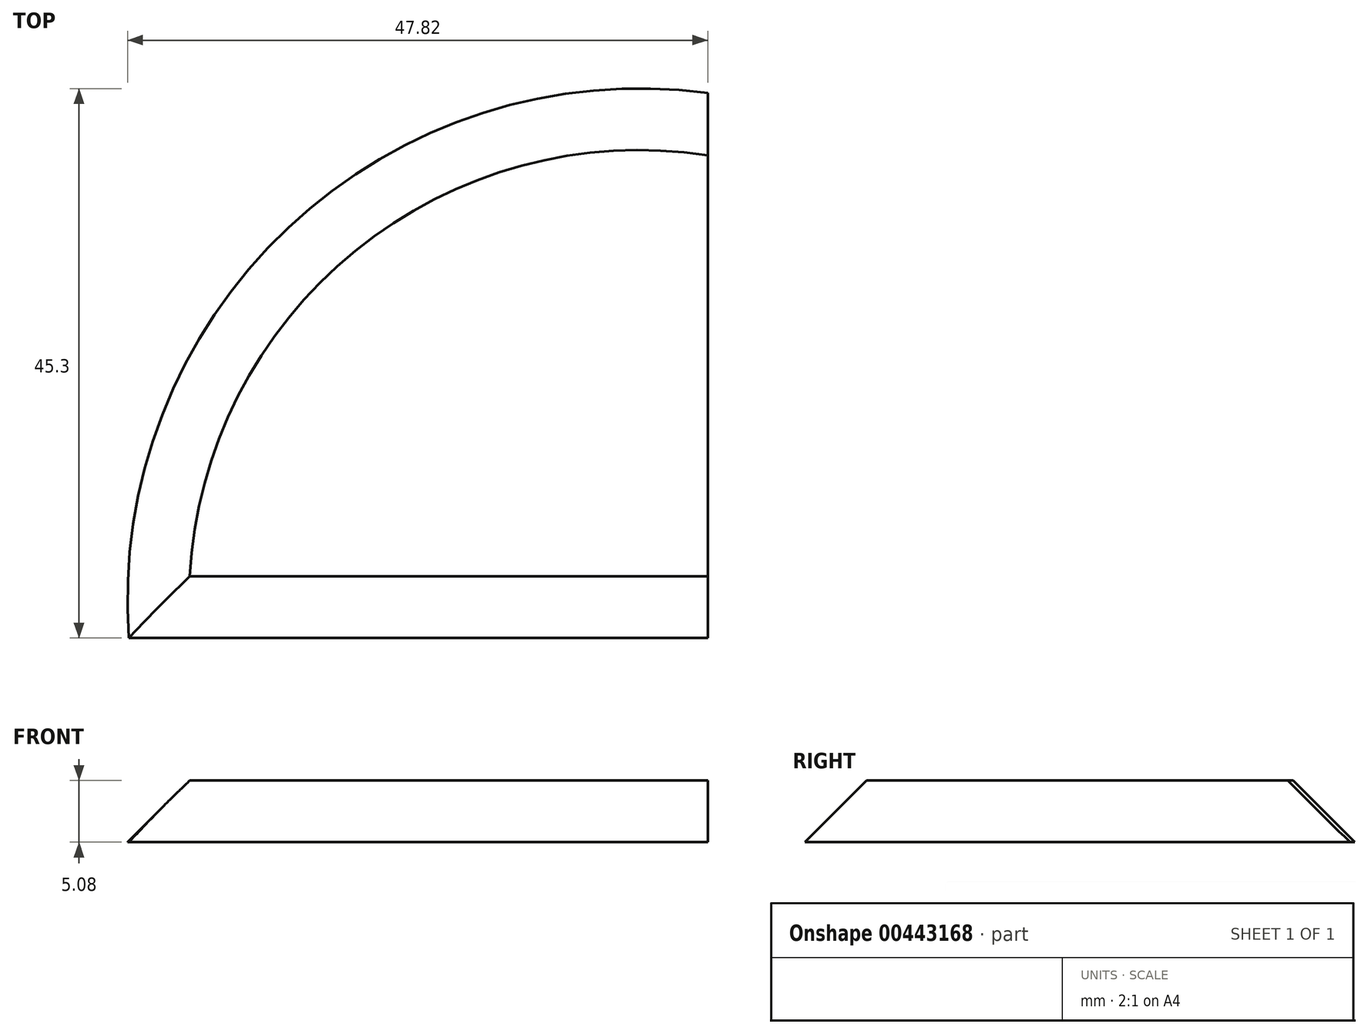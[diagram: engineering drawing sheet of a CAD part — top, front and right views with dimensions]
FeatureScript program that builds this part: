
annotation { "Feature Type Name" : "Feature", "Feature Type Description" : "" }
export const myFeature = defineFeature(function(context is Context, id is Id, definition is map)
    precondition{}
    {
        {
            var Q0;
            Q0=qCreatedBy(makeId("Top.planeOp"),FACE);
            var sketch = newSketch(context, id + "F0", { "sketchPlane" : qUnion([Q0])});
            skArc(sketch, "E0", {"start": v(0, 44.92) * mm, "mid": v(-34.56, 33.84) * mm, "end": v(-47.7, 0) * mm});
            skLineSegment(sketch, "E1", {"start": v(0, 44.92) * mm, "end": v(0, 0) * mm});
            skLineSegment(sketch, "E2", {"start": v(0, 0) * mm, "end": v(-47.7, 0) * mm});
            skSolve(sketch);
        }
        {
            var Q0;
            Q0 = qSketchRegion(id + "F0", true);
            extrude(context, id + "F1", {"entities" : qUnion([Q0]), "depth" : 5.08 * mm});
        }
        {
            var Q0;
            Q0=makeQuery(id+"F1.opExtrude","CAP_EDGE",EDGE,{"disambiguationData":[OSD([sQuery(id+"F0.wireOp",EDGE,"E0")])],"isStart":false});
            var Q1;
            Q1=makeQuery(id+"F1.opExtrude","CAP_EDGE",EDGE,{"disambiguationData":[OSD([sQuery(id+"F0.wireOp",EDGE,"E2")])],"isStart":false});
            chamfer(context, id + "F2", {"entities" : qUnion([Q0, Q1]), "width" : 5.08 * mm, "tangentPropagation" : true});
        }
    });
